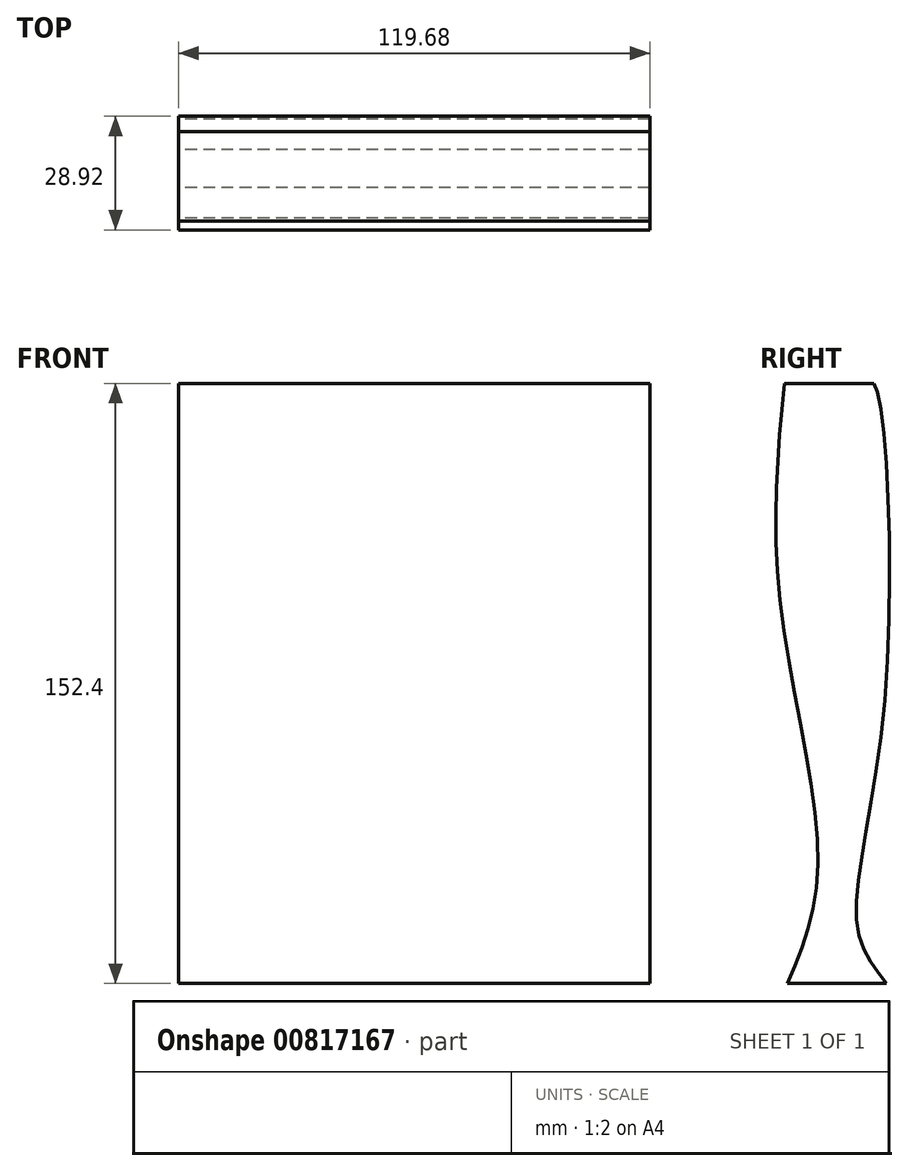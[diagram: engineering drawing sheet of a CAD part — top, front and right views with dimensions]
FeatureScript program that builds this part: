
annotation { "Feature Type Name" : "Feature", "Feature Type Description" : "" }
export const myFeature = defineFeature(function(context is Context, id is Id, definition is map)
    precondition{}
    {
        {
            var Q0;
            Q0=qCreatedBy(makeId("Top.planeOp"),FACE);
            var sketch = newSketch(context, id + "F0", { "sketchPlane" : qUnion([Q0])});
            skLineSegment(sketch, "E0.bottom", {"start": v(-59.84, -23.37) * mm, "end": v(59.84, -23.37) * mm});
            skLineSegment(sketch, "E0.top", {"start": v(-59.84, 23.37) * mm, "end": v(59.84, 23.37) * mm});
            skLineSegment(sketch, "E0.left", {"start": v(-59.84, -23.37) * mm, "end": v(-59.84, 23.37) * mm});
            skLineSegment(sketch, "E0.right", {"start": v(59.84, -23.37) * mm, "end": v(59.84, 23.37) * mm});
            skPoint(sketch, "E0.middle", {"position": v(0, 0) * mm});
            skSolve(sketch);
        }
        {
            var Q0;
            Q0 = qSketchRegion(id + "F0", true);
            extrude(context, id + "F1", {"entities" : qUnion([Q0]), "depth" : 152.4 * mm, "offsetDistance" : 25.4 * mm});
        }
        {
            var Q0;
            Q0=makeQuery(id+"F1.opExtrude","SWEPT_FACE",FACE,{"disambiguationData":[OSD([sQuery(id+"F0.wireOp",EDGE,"E0.left")])]});
            var sketch = newSketch(context, id + "F2", { "sketchPlane" : qUnion([Q0])});
            skFitSpline(sketch, "E1", {"points": [v(-11.4, 0) * mm, v(-4.05, 13.81) * mm, v(-10.84, 71.11) * mm, v(-8.2, 152.4) * mm, v(-7.07, 152.4) * mm], "startDerivative": vector(52.23, 64.93) * mm, "endDerivative": vector(23.21, -11.9) * mm});
            skSolve(sketch);
        }
        {
            var Q0;
            {var subQ1=sQuery(id+"F0.wireOp",EDGE,"E0.left");var subQ6=makeQuery(id+"F1.opExtrude","SWEPT_EDGE",EDGE,{"disambiguationData":[OSD([sQuery(id+"F0.wireOp",EDGE,"E0.top"),subQ1])]});Q0=makeQuery(id+"F2.imprint","IMPRINT",FACE,{"disambiguationData":[TD([[makeQuery(id+"F2.imprint","IMPRINT",EDGE,{"derivedFrom":subQ6}),1.0]])]});}
            extrude(context, id + "F3", {"entities" : qUnion([Q0]), "operationType" : NewBodyOperationType.REMOVE, "oppositeDirection" : true, "depth" : 152.4 * mm, "offsetDistance" : 25.4 * mm});
        }
        {
            var Q0;
            Q0=makeQuery(id+"F1.opExtrude","SWEPT_FACE",FACE,{"disambiguationData":[OSD([sQuery(id+"F0.wireOp",EDGE,"E0.left")])]});
            var sketch = newSketch(context, id + "F4", { "sketchPlane" : qUnion([Q0])});
            skPoint(sketch, "E2.1.internal.snap0", {"position": v(5.98, 0) * mm});
            skFitSpline(sketch, "E2", {"points": [v(13.75, 0) * mm, v(5.98, 30.7) * mm, v(15.65, 96.9) * mm, v(14.55, 152.4) * mm], "startDerivative": vector(-43, 102.81) * mm, "endDerivative": vector(-14.6, 150.54) * mm});
            skSolve(sketch);
        }
        {
            var Q0;
            {var subQ0=sQuery(id+"F4.wireOp",EDGE,"E2");Q0=makeQuery(id+"F4.imprint","IMPRINT",FACE,{"disambiguationData":[TD([[makeQuery(id+"F4.imprint","IMPRINT",EDGE,{"derivedFrom":subQ0}),-1.0]])]});}
            extrude(context, id + "F5", {"entities" : qUnion([Q0]), "operationType" : NewBodyOperationType.REMOVE, "oppositeDirection" : true, "depth" : 127 * mm, "offsetDistance" : 25.4 * mm});
        }
    });
